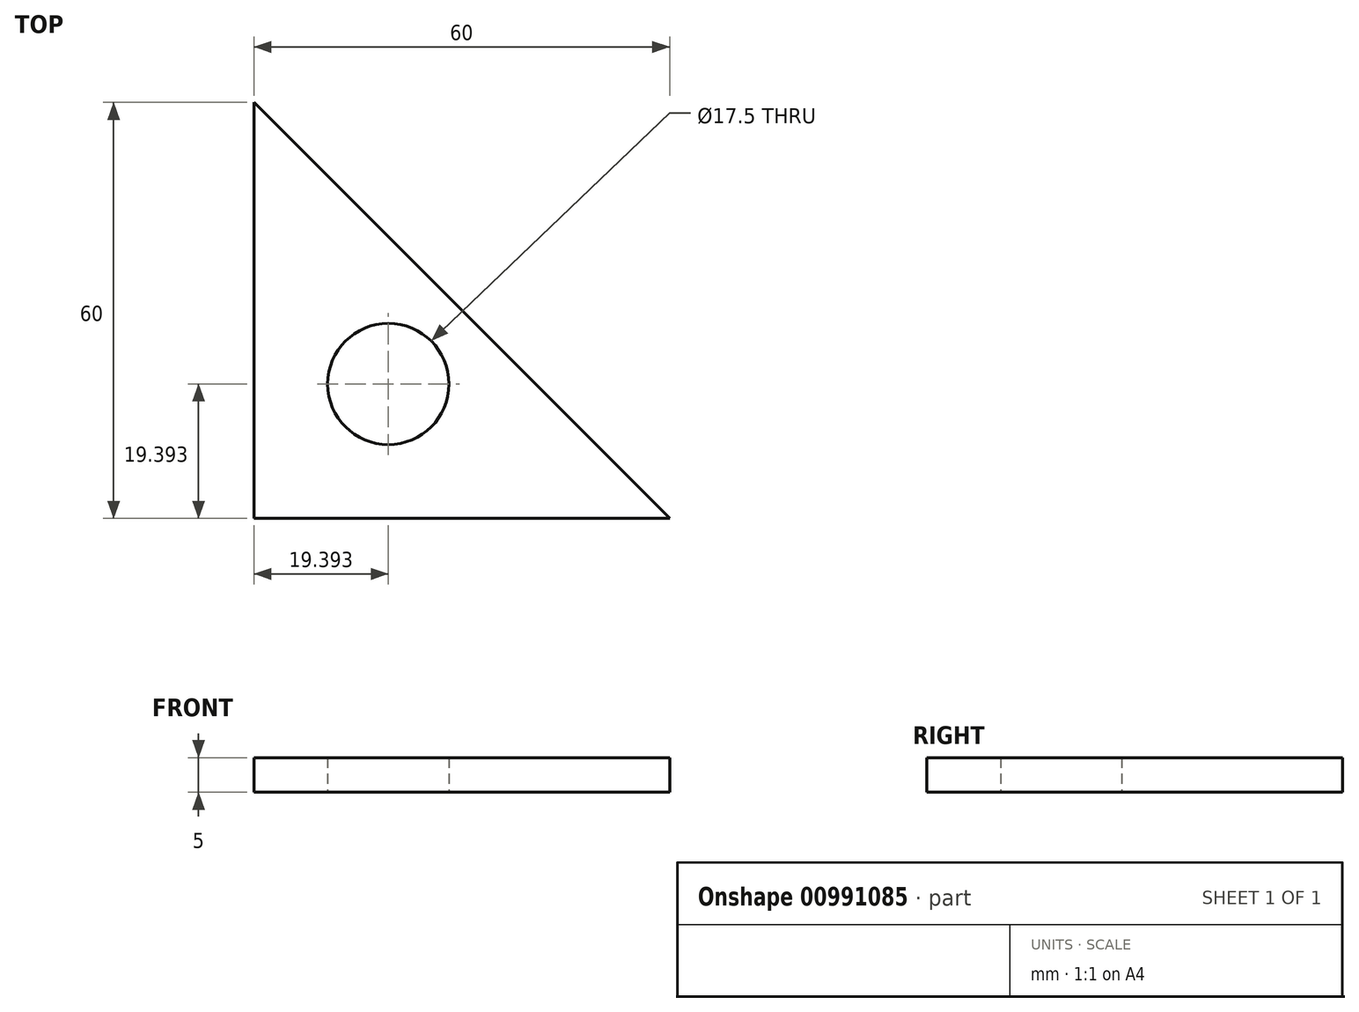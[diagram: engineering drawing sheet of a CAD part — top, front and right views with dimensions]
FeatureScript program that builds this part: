
annotation { "Feature Type Name" : "Feature", "Feature Type Description" : "" }
export const myFeature = defineFeature(function(context is Context, id is Id, definition is map)
    precondition{}
    {
        {
            var Q0;
            Q0=qCreatedBy(makeId("Top.planeOp"),FACE);
            var sketch = newSketch(context, id + "F0", { "sketchPlane" : qUnion([Q0])});
            skLineSegment(sketch, "E0", {"start": v(0, 0) * mm, "end": v(0, 60) * mm});
            skLineSegment(sketch, "E1", {"start": v(0, 0) * mm, "end": v(60, 0) * mm});
            skLineSegment(sketch, "E2", {"start": v(60, 0) * mm, "end": v(0, 60) * mm});
            skCircle(sketch, "E3", {"center": v(19.4, 19.4) * mm, "radius": 3.5 * mm});
            skLineSegment(sketch, "E4", {"start": v(30, 30) * mm, "end": v(19.4, 19.4) * mm});
            skSolve(sketch);
        }
        {
            var Q0;
            {var subQ1=sQuery(id+"F0.wireOp",EDGE,"E0");Q0=makeQuery(id+"F0.imprint","IMPRINT",FACE,{"disambiguationData":[TD([[makeQuery(id+"F0.imprint","IMPRINT",EDGE,{"derivedFrom":subQ1}),-1.0]])]});}
            extrude(context, id + "F1", {"entities" : qUnion([Q0]), "depth" : 5 * mm, "offsetDistance" : 25 * mm});
        }
        {
            var Q0;
            Q0=sQuery(id+"F0.wireOp",VERTEX,"E4.end");
            var Q1;
            Q1=makeQuery(id+"F1.opExtrude","SWEPT_BODY",BODY,{"disambiguationData":[OSD([sQuery(id+"F0.wireOp",EDGE,"E0"),sQuery(id+"F0.wireOp",EDGE,"E1"),sQuery(id+"F0.wireOp",EDGE,"E2"),sQuery(id+"F0.wireOp",EDGE,"E3")])]});
            hole(context, id + "F2", {"style" : HoleStyle.SIMPLE, "endStyle" : HoleEndStyle.BLIND, "oppositeDirection" : true, "standardTappedOrClearance" : lookupTablePath({ "fit" : "Normal", "standard" : "ISO", "size" : "M16", "type" : "Clearance" }), "standardBlindInLast" : lookupTablePath({ "fit" : "Normal", "standard" : "ISO", "engagement" : "75%", "pitch" : "2 mm", "size" : "M16", "type" : "Clearance & tapped" }), "holeDiameter" : 17.5 * mm, "majorDiameter" : 5 * mm, "holeDepth" : 203 * mm, "isTappedThrough" : true, "tappedDepth" : 5 * mm, "tapClearance" : 3, "locations" : qUnion([Q0]), "scope" : qUnion([Q1])});
        }
    });
